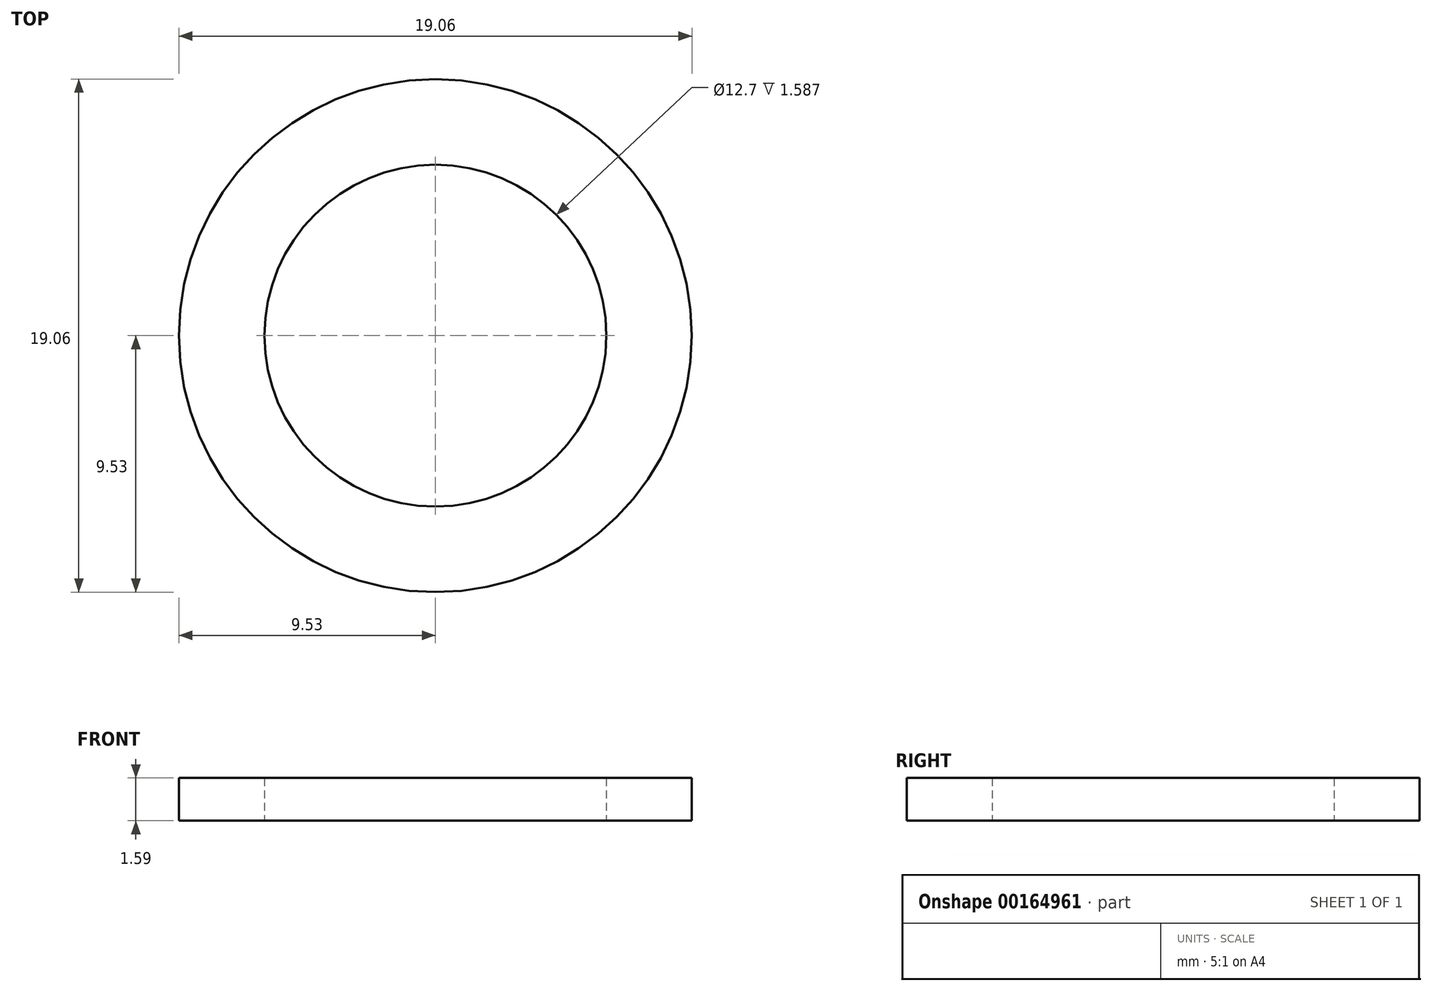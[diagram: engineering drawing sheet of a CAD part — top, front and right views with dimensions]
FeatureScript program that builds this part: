
annotation { "Feature Type Name" : "Feature", "Feature Type Description" : "" }
export const myFeature = defineFeature(function(context is Context, id is Id, definition is map)
    precondition{}
    {
        {
            var Q0;
            Q0=qCreatedBy(makeId("Top.planeOp"),FACE);
            var sketch = newSketch(context, id + "F0", { "sketchPlane" : qUnion([Q0])});
            skCircle(sketch, "E0", {"center": v(0, 0) * mm, "radius": 6.35 * mm});
            skCircle(sketch, "E1", {"center": v(0, 0) * mm, "radius": 9.53 * mm});
            skSolve(sketch);
        }
        {
            var Q0;
            Q0 = qSketchRegion(id + "F0", true);
            extrude(context, id + "F1", {"entities" : qUnion([Q0]), "depth" : 1.59 * mm});
        }
    });
